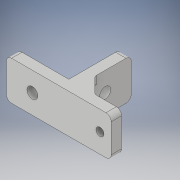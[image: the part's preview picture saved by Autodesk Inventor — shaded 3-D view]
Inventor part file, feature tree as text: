
AUTODESK INVENTOR PART (.ipt)
format: ipt  version: 2018 (Build 220112000, 112)  size: 177,152 bytes
history: native  units: in
note: dims shown in document units (in); Inventor stores cm internally (conversion verified against a paired STEP export)
features: sketch x7, extrude x6, fillet x3, projected_geometry x2, mirror x1
ambient origin geometry x8: Origin, YZ Plane, XZ Plane, XY Plane, X Axis, Y Axis, Z Axis, Center Point
bodies: Solid1 (feature_tree)
feature tree (19):
  extrude  "Extrusion1"  Depth=0.1575in
  extrude  "Extrusion2"  Depth=0.1575in
  extrude  "Extrusion3"  Depth=0.5906in TaperAngle=0.0deg
  extrude  "Extrusion4"  Depth=0.5906in TaperAngle=0.0deg
  extrude  "Extrusion5"  Depth=0.5906in TaperAngle=0.0deg
  mirror  "Mirror1"
  fillet  "Fillet1"  Radius=0.122in
  sketch  "Sketch6"  dims[d14=0.315in d15=0.5906in d16=0.0in d17=0.2362in d18=0.2362in]
  extrude  "Extrusion6"  Depth=0.5906in TaperAngle=0.0deg
  fillet  "Fillet2"  Radius=0.2362in
  fillet  "Fillet3"  Radius=0.2362in
  sketch  "Sketch1"  dims[d0=0.7874in d1=0.1575in]
  sketch  "Sketch2"  dims[d2=0.7874in d3=0.1575in]
  projected_geometry  "Projected Loop1"
  sketch  "Sketch3"  dims[d4=0.7874in d5=0.5906in d6=0.0in]
  projected_geometry  "Projected Loop2"
  sketch  "Sketch4"  dims[d7=0.1654in d8=0.5906in d9=0.0in]
  sketch  "Sketch5"  dims[d10=0.1654in d11=0.5906in d12=0.0in d13=0.122in]
  sketch  "Sketch7"  dims[d19=0.1181in d20=0.0in d21=0.0787in d22=0.1575in d23=0.0in d24=0.0787in d25=0.0787in]
